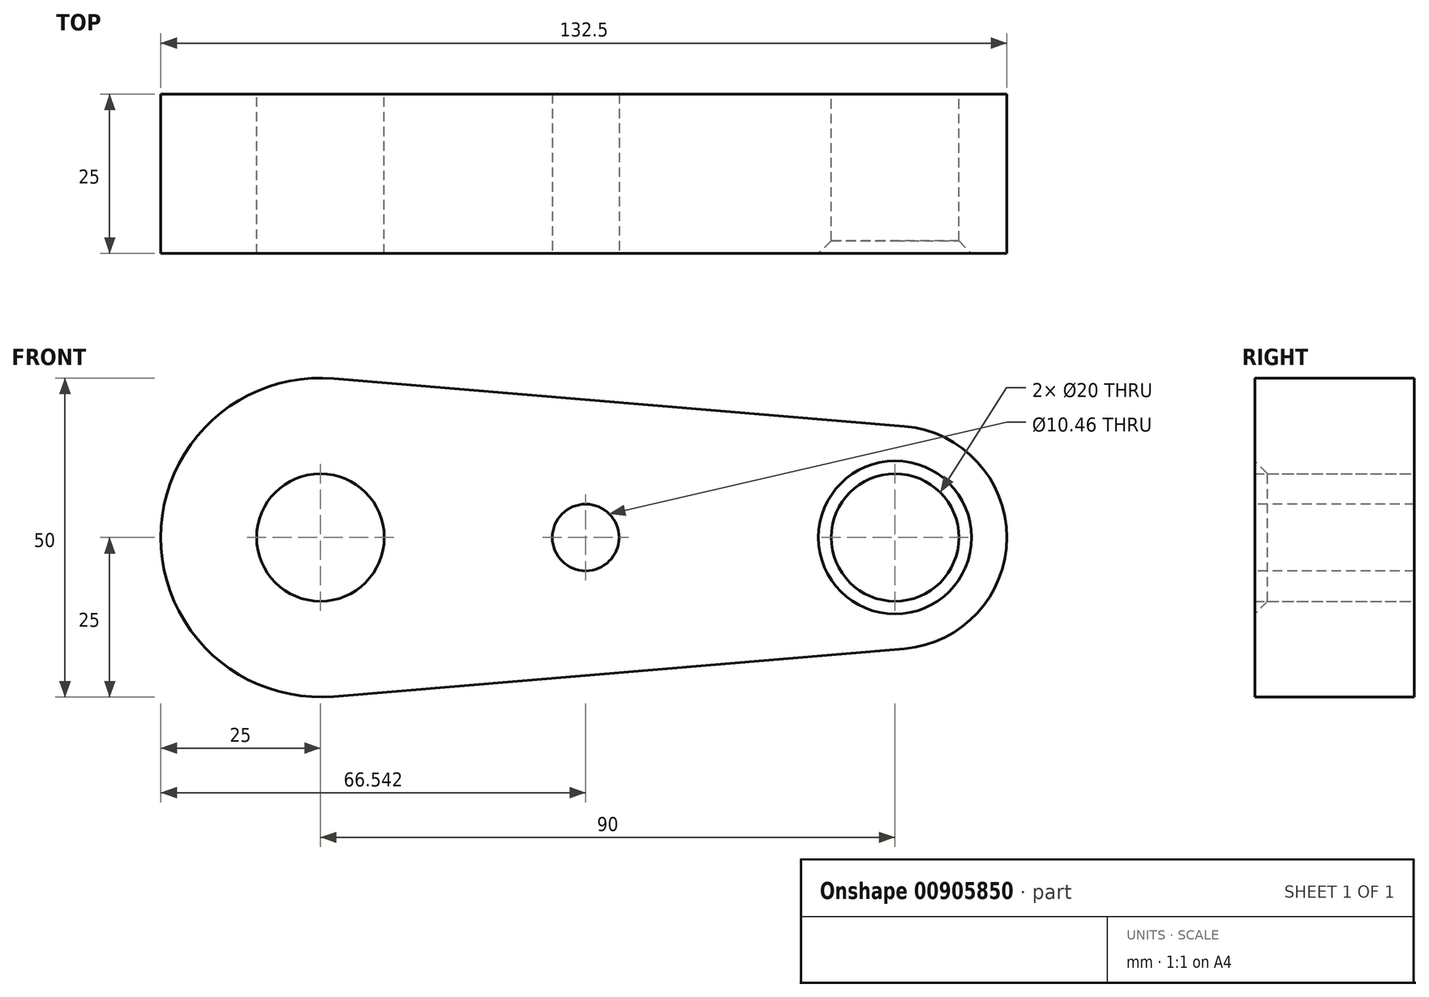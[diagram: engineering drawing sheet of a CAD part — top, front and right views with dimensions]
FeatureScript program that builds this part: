
annotation { "Feature Type Name" : "Feature", "Feature Type Description" : "" }
export const myFeature = defineFeature(function(context is Context, id is Id, definition is map)
    precondition{}
    {
        {
            var Q0;
            Q0=qCreatedBy(makeId("Front.planeOp"),FACE);
            var sketch = newSketch(context, id + "F0", { "sketchPlane" : qUnion([Q0])});
            skCircle(sketch, "E0", {"center": v(0, 0) * mm, "radius": 25 * mm});
            skCircle(sketch, "E1", {"center": v(90, 0) * mm, "radius": 17.5 * mm});
            skLineSegment(sketch, "E2", {"start": v(2.08, 24.91) * mm, "end": v(91.46, 17.44) * mm});
            skLineSegment(sketch, "E3", {"start": v(2.08, -24.91) * mm, "end": v(91.46, -17.44) * mm});
            skCircle(sketch, "E4", {"center": v(0, 0) * mm, "radius": 10 * mm});
            skCircle(sketch, "E5", {"center": v(90, 0) * mm, "radius": 10 * mm});
            skSolve(sketch);
        }
        {
            var Q0;
            Q0=qSketchRegion(id+"F0",true);
            extrude(context, id + "F1", {"entities" : qUnion([Q0]), "depth" : 25 * mm});
        }
        {
            var Q0;
            Q0=makeQuery(id+"Fcgcib3Fz2EW007_1.opExtrude","CAP_EDGE",EDGE,{"disambiguationData":[OSD([sQuery(id+"F0.wireOp",EDGE,"E0")])],"isStart":false});
            var Q1;
            Q1=makeQuery(id+"Fcgcib3Fz2EW007_1.opExtrude","CAP_EDGE",EDGE,{"disambiguationData":[OSD([sQuery(id+"F0.wireOp",EDGE,"E4")])],"isStart":false});
            var Q2;
            Q2=makeQuery(id+"F1.opExtrude","CAP_EDGE",EDGE,{"disambiguationData":[OSD([sQuery(id+"F0.wireOp",EDGE,"E5")])],"isStart":false});
            chamfer(context, id + "F2", {"entities" : qUnion([Q0, Q1, Q2]), "width" : 2 * mm, "tangentPropagation" : true});
        }
        {
            var Q0;
            Q0=qCreatedBy(makeId("Front.planeOp"),FACE);
            var sketch = newSketch(context, id + "F3", { "sketchPlane" : qUnion([Q0])});
            skCircle(sketch, "E6", {"center": v(43.7, 0) * mm, "radius": 10.84 * mm});
            skSolve(sketch);
        }
        {
            var Q0;
            Q0=makeQuery(id+"F1.opExtrude","CAP_FACE",FACE,{"disambiguationData":[OSD([sQuery(id+"F0.wireOp",EDGE,"E0"),sQuery(id+"F0.wireOp",EDGE,"E1"),sQuery(id+"F0.wireOp",EDGE,"E2"),sQuery(id+"F0.wireOp",EDGE,"E3"),sQuery(id+"F0.wireOp",EDGE,"E4"),sQuery(id+"F0.wireOp",EDGE,"E5")])],"isStart":false});
            var Q1;
            Q1=sQuery(id+"F3.wireOp",EDGE,"E6");
            extrude(context, id + "F4", {"entities" : qUnion([Q0]), "bodyType" : ToolBodyType.SURFACE, "surfaceEntities" : qUnion([Q1]), "endBound" : BoundingType.THROUGH_ALL, "depth" : 25 * mm, "offsetDistance" : 25 * mm});
        }
        {
            var Q0;
            Q0=makeQuery(id+"F4.opExtrude","SWEPT_BODY",BODY,{"disambiguationData":[OSD([sQuery(id+"F3.wireOp",EDGE,"E6")])]});
            deleteBodies(context, id + "F5", {"entities" : qUnion([Q0])});
        }
        {
            var Q0;
            Q0=makeQuery(id+"F1.opExtrude","CAP_FACE",FACE,{"disambiguationData":[OSD([sQuery(id+"F0.wireOp",EDGE,"E0"),sQuery(id+"F0.wireOp",EDGE,"E1"),sQuery(id+"F0.wireOp",EDGE,"E2"),sQuery(id+"F0.wireOp",EDGE,"E3"),sQuery(id+"F0.wireOp",EDGE,"E4"),sQuery(id+"F0.wireOp",EDGE,"E5")])],"isStart":false});
            var sketch = newSketch(context, id + "F6", { "sketchPlane" : qUnion([Q0])});
            skCircle(sketch, "E7", {"center": v(41.54, 0) * mm, "radius": 5.23 * mm});
            skSolve(sketch);
        }
        {
            var Q0;
            Q0=makeQuery(id+"F6.imprint","IMPRINT",FACE,{"disambiguationData":[TD([[makeQuery(id+"F6.imprint","IMPRINT",EDGE,{"derivedFrom":sQuery(id+"F6.wireOp",EDGE,"E7")}),1.0]])]});
            var Q1;
            Q1=sQuery(id+"F6.wireOp",EDGE,"E7");
            extrude(context, id + "F7", {"entities" : qUnion([Q0]), "operationType" : NewBodyOperationType.REMOVE, "surfaceEntities" : qUnion([Q1]), "oppositeDirection" : true, "depth" : 25 * mm, "offsetDistance" : 25 * mm});
        }
    });
